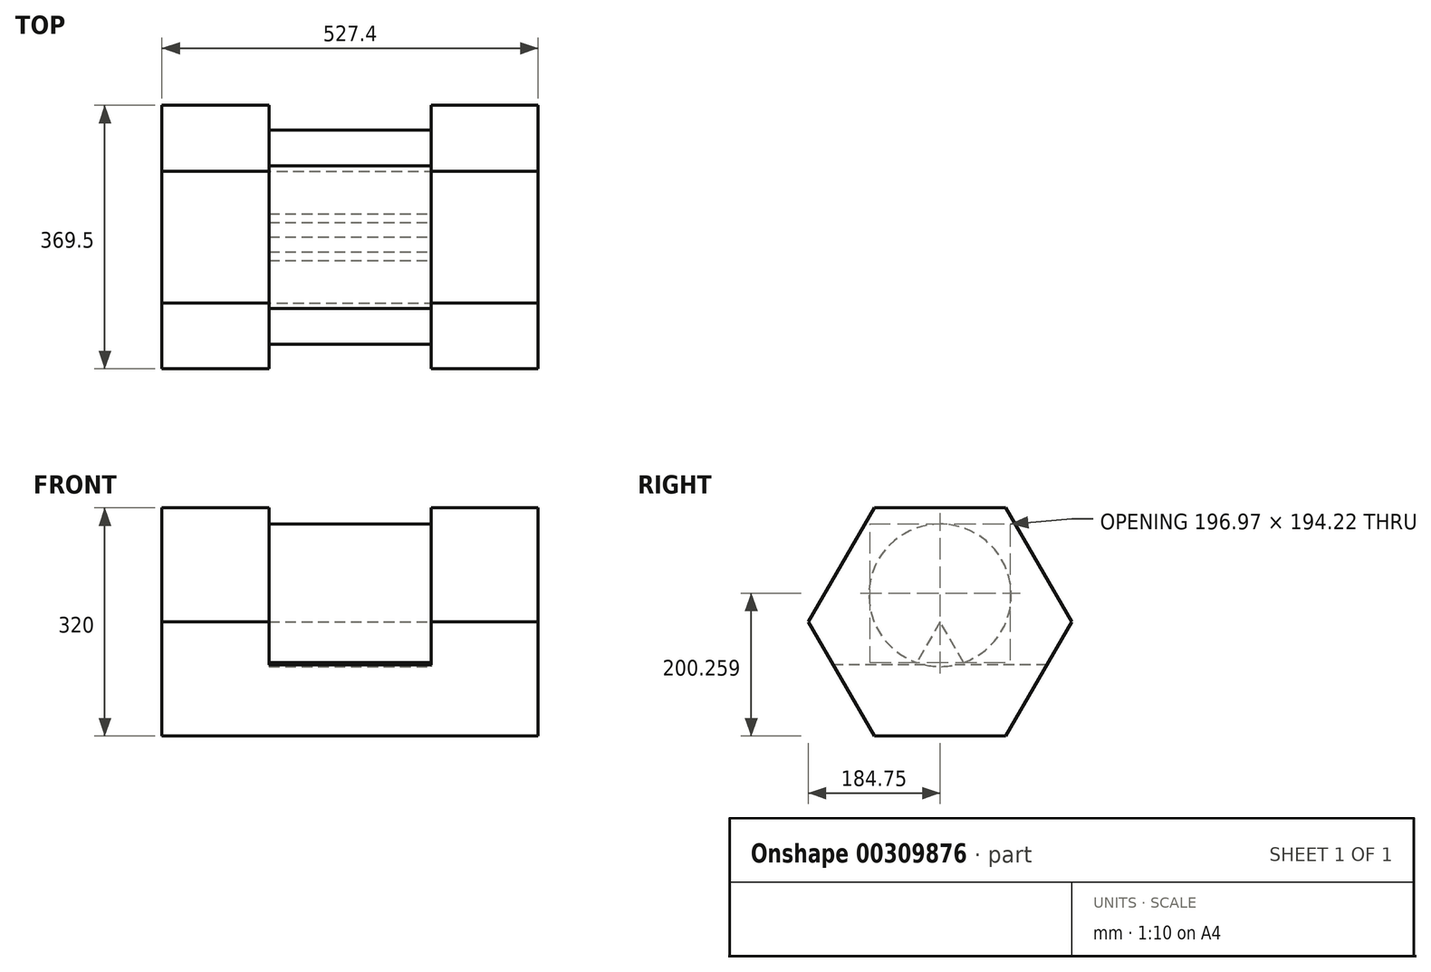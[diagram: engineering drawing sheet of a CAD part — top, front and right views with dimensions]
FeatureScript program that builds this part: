
annotation { "Feature Type Name" : "Feature", "Feature Type Description" : "" }
export const myFeature = defineFeature(function(context is Context, id is Id, definition is map)
    precondition{}
    {
        {
            var Q0;
            Q0=qCreatedBy(makeId("Top.planeOp"),FACE);
            var sketch = newSketch(context, id + "F0", { "sketchPlane" : qUnion([Q0])});
            skLineSegment(sketch, "E0.bottom", {"start": v(463.7, -463.7) * mm, "end": v(-463.7, -463.7) * mm});
            skLineSegment(sketch, "E0.top", {"start": v(463.7, 463.7) * mm, "end": v(-463.7, 463.7) * mm});
            skLineSegment(sketch, "E0.left", {"start": v(463.7, -463.7) * mm, "end": v(463.7, 463.7) * mm});
            skLineSegment(sketch, "E0.right", {"start": v(-463.7, -463.7) * mm, "end": v(-463.7, 463.7) * mm});
            skPoint(sketch, "E0.middle", {"position": v(0, 0) * mm});
            skLineSegment(sketch, "E1", {"start": v(-263.7, -463.7) * mm, "end": v(-263.7, 463.7) * mm});
            skLineSegment(sketch, "E2", {"start": v(263.7, -463.7) * mm, "end": v(263.7, 463.7) * mm});
            skLineSegment(sketch, "E3", {"start": v(-463.7, 263.7) * mm, "end": v(463.7, 263.7) * mm});
            skLineSegment(sketch, "E4", {"start": v(463.7, -263.7) * mm, "end": v(-463.7, -263.7) * mm});
            skSolve(sketch);
        }
        {
            var Q0;
            Q0=sQuery(id+"F0.wireOp",EDGE,"E2");
            cPlane(context, id + "F1", {"entities" : qUnion([Q0]), "cplaneType" : CPlaneType.LINE_ANGLE, "offset" : 25 * mm, "angle" : 90 * degree, "width" : 150 * mm, "height" : 150 * mm});
        }
        {
            var Q0;
            Q0=qCreatedBy(id+"F1.planeOp",FACE);
            var sketch = newSketch(context, id + "F2", { "sketchPlane" : qUnion([Q0])});
            skPoint(sketch, "E5", {"position": v(0, 0) * mm});
            skPoint(sketch, "E6", {"position": v(1245.8, -121.93) * mm});
            skPoint(sketch, "E7.0", {"position": v(-263.7, 0) * mm});
            skPoint(sketch, "E8.0", {"position": v(263.7, 0) * mm});
            skPoint(sketch, "E9", {"position": v(131.85, 0) * mm});
            skLineSegment(sketch, "E10", {"start": v(0, 0) * mm, "end": v(0, 320) * mm});
            skCircle(sketch, "E11.cCircle", {"center": v(0, 160) * mm, "radius": 160 * mm, "construction": true});
            skLineSegment(sketch, "E11.0", {"start": v(92.38, 0) * mm, "end": v(-92.38, 0) * mm});
            skLineSegment(sketch, "E11.1", {"start": v(-92.38, 0) * mm, "end": v(-184.75, 160) * mm});
            skLineSegment(sketch, "E11.2", {"start": v(-184.75, 160) * mm, "end": v(-92.38, 320) * mm});
            skLineSegment(sketch, "E11.3", {"start": v(-92.38, 320) * mm, "end": v(92.38, 320) * mm});
            skLineSegment(sketch, "E11.4", {"start": v(92.38, 320) * mm, "end": v(184.75, 160) * mm});
            skLineSegment(sketch, "E11.5", {"start": v(184.75, 160) * mm, "end": v(92.38, 0) * mm});
            skSolve(sketch);
        }
        {
            var Q0;
            {var subQ2=sQuery(id+"F2.wireOp",EDGE,"E10");Q0=makeQuery(id+"F2.imprint","IMPRINT",FACE,{"disambiguationData":[TD([[makeQuery(id+"F2.imprint","IMPRINT",EDGE,{"derivedFrom":subQ2}),-1.0]])]});}
            var Q1;
            {var subQ3=sQuery(id+"F2.wireOp",EDGE,"E10");Q1=makeQuery(id+"F2.imprint","IMPRINT",FACE,{"disambiguationData":[TD([[makeQuery(id+"F2.imprint","IMPRINT",EDGE,{"derivedFrom":subQ3}),1.0]])]});}
            extrude(context, id + "F3", {"entities" : qUnion([Q0, Q1]), "oppositeDirection" : true, "depth" : 150 * mm});
        }
        {
            var Q0;
            Q0=makeQuery(id+"F3.opExtrude","SWEPT_BODY",BODY,{"disambiguationData":[OSD([sQuery(id+"F2.wireOp",EDGE,"E11.0"),sQuery(id+"F2.wireOp",EDGE,"E11.1"),sQuery(id+"F2.wireOp",EDGE,"E11.2"),sQuery(id+"F2.wireOp",EDGE,"E11.3"),sQuery(id+"F2.wireOp",EDGE,"E11.4"),sQuery(id+"F2.wireOp",EDGE,"E11.5")])]});
            var Q1;
            Q1=qCreatedBy(makeId("Right.planeOp"),FACE);
            mirror(context, id + "F4", {"entities" : qUnion([Q0]), "mirrorPlane" : qUnion([Q1])});
        }
        {
            var Q0;
            Q0=makeQuery(id+"F3.opExtrude","CAP_FACE",FACE,{"disambiguationData":[OSD([sQuery(id+"F2.wireOp",EDGE,"E11.0"),sQuery(id+"F2.wireOp",EDGE,"E11.1"),sQuery(id+"F2.wireOp",EDGE,"E11.2"),sQuery(id+"F2.wireOp",EDGE,"E11.3"),sQuery(id+"F2.wireOp",EDGE,"E11.4"),sQuery(id+"F2.wireOp",EDGE,"E11.5")])],"isStart":false});
            var sketch = newSketch(context, id + "F5", { "sketchPlane" : qUnion([Q0])});
            skLineSegment(sketch, "E12", {"start": v(-92.38, 0) * mm, "end": v(92.38, 320) * mm});
            skLineSegment(sketch, "E13", {"start": v(-184.75, 160) * mm, "end": v(184.75, 160) * mm});
            skPoint(sketch, "E14", {"position": v(0, 160) * mm});
            skLineSegment(sketch, "E15", {"start": v(0, 160) * mm, "end": v(92.38, 0) * mm});
            skLineSegment(sketch, "E16", {"start": v(0, 160) * mm, "end": v(0, 320) * mm});
            skLineSegment(sketch, "E17", {"start": v(-150, 99.8) * mm, "end": v(150, 99.8) * mm});
            skPoint(sketch, "E18", {"position": v(0, 197.49) * mm});
            skCircle(sketch, "E19", {"center": v(0, 197.49) * mm, "radius": 99.88 * mm});
            skSolve(sketch);
        }
        {
            var Q0;
            {var subQ1=makeQuery(id+"F3.opExtrude","CAP_EDGE",EDGE,{"disambiguationData":[OSD([sQuery(id+"F2.wireOp",EDGE,"E11.5")])],"isStart":false});var subQ3=sQuery(id+"F5.wireOp",EDGE,"E17");var subQ5=makeQuery(id+"F5.imprint","INTERSECT",VERTEX,{"derivedFrom":[subQ1,subQ3]});Q0=makeQuery(id+"F5.imprint","IMPRINT",FACE,{"disambiguationData":[TD([[makeQuery(id+"F5.imprint","IMPRINT",EDGE,{"disambiguationData":[TD([[subQ5,-1.0]])],"derivedFrom":subQ3}),-1.0]])]});}
            var Q1;
            {var subQ1=makeQuery(id+"F3.opExtrude","CAP_EDGE",EDGE,{"disambiguationData":[OSD([sQuery(id+"F2.wireOp",EDGE,"E11.0")])],"isStart":false});Q1=makeQuery(id+"F5.imprint","IMPRINT",FACE,{"disambiguationData":[TD([[makeQuery(id+"F5.imprint","IMPRINT",EDGE,{"derivedFrom":subQ1}),1.0]])]});}
            var Q2;
            {var subQ1=makeQuery(id+"F3.opExtrude","CAP_EDGE",EDGE,{"disambiguationData":[OSD([sQuery(id+"F2.wireOp",EDGE,"E11.1")])],"isStart":false});var subQ3=sQuery(id+"F5.wireOp",EDGE,"E17");var subQ5=makeQuery(id+"F5.imprint","INTERSECT",VERTEX,{"derivedFrom":[subQ1,subQ3]});Q2=makeQuery(id+"F5.imprint","IMPRINT",FACE,{"disambiguationData":[TD([[makeQuery(id+"F5.imprint","IMPRINT",EDGE,{"disambiguationData":[TD([[subQ5,1.0]])],"derivedFrom":subQ3}),-1.0]])]});}
            var Q3;
            Q3=makeQuery(id+"F4.opPattern","COPY",FACE,{"derivedFrom":makeQuery(id+"F3.opExtrude","CAP_FACE",FACE,{"disambiguationData":[OSD([sQuery(id+"F2.wireOp",EDGE,"E11.0"),sQuery(id+"F2.wireOp",EDGE,"E11.1"),sQuery(id+"F2.wireOp",EDGE,"E11.2"),sQuery(id+"F2.wireOp",EDGE,"E11.3"),sQuery(id+"F2.wireOp",EDGE,"E11.4"),sQuery(id+"F2.wireOp",EDGE,"E11.5")])],"isStart":false}),"instanceName":"1"});
            extrude(context, id + "F6", {"entities" : qUnion([Q0, Q1, Q2]), "operationType" : NewBodyOperationType.ADD, "endBound" : BoundingType.UP_TO_SURFACE, "endBoundEntityFace" : qUnion([Q3]), "depth" : 25 * mm});
        }
        {
            var Q0;
            {var subQ1=sQuery(id+"F5.wireOp",EDGE,"E13");var subQ3=sQuery(id+"F5.wireOp",EDGE,"E19");var subQ4=makeQuery(id+"F5.imprint","INTERSECT",VERTEX,{"disambiguationData":[OD(0.0)],"derivedFrom":[subQ1,subQ3]});Q0=makeQuery(id+"F5.imprint","IMPRINT",FACE,{"disambiguationData":[TD([[makeQuery(id+"F5.imprint","IMPRINT",EDGE,{"disambiguationData":[TD([[subQ4,1.0]])],"derivedFrom":subQ3}),1.0]])]});}
            var Q1;
            {var subQ1=sQuery(id+"F5.wireOp",EDGE,"E12");var subQ3=sQuery(id+"F5.wireOp",EDGE,"E19");var subQ4=makeQuery(id+"F5.imprint","INTERSECT",VERTEX,{"disambiguationData":[OD(1.0)],"derivedFrom":[subQ1,subQ3]});Q1=makeQuery(id+"F5.imprint","IMPRINT",FACE,{"disambiguationData":[TD([[makeQuery(id+"F5.imprint","IMPRINT",EDGE,{"disambiguationData":[TD([[subQ4,-1.0]])],"derivedFrom":subQ3}),1.0]])]});}
            var Q2;
            {var subQ1=sQuery(id+"F5.wireOp",EDGE,"E12");var subQ3=sQuery(id+"F5.wireOp",EDGE,"E19");var subQ4=makeQuery(id+"F5.imprint","INTERSECT",VERTEX,{"disambiguationData":[OD(1.0)],"derivedFrom":[subQ1,subQ3]});Q2=makeQuery(id+"F5.imprint","IMPRINT",FACE,{"disambiguationData":[TD([[makeQuery(id+"F5.imprint","IMPRINT",EDGE,{"disambiguationData":[TD([[subQ4,1.0]])],"derivedFrom":subQ3}),1.0]])]});}
            var Q3;
            {var subQ1=sQuery(id+"F5.wireOp",EDGE,"E13");var subQ3=sQuery(id+"F5.wireOp",EDGE,"E19");var subQ4=makeQuery(id+"F5.imprint","INTERSECT",VERTEX,{"disambiguationData":[OD(1.0)],"derivedFrom":[subQ1,subQ3]});Q3=makeQuery(id+"F5.imprint","IMPRINT",FACE,{"disambiguationData":[TD([[makeQuery(id+"F5.imprint","IMPRINT",EDGE,{"disambiguationData":[TD([[subQ4,1.0]])],"derivedFrom":subQ3}),1.0]])]});}
            var Q4;
            {var subQ1=sQuery(id+"F5.wireOp",EDGE,"E12");var subQ3=sQuery(id+"F5.wireOp",EDGE,"E19");var subQ4=makeQuery(id+"F5.imprint","INTERSECT",VERTEX,{"disambiguationData":[OD(0.0)],"derivedFrom":[subQ1,subQ3]});Q4=makeQuery(id+"F5.imprint","IMPRINT",FACE,{"disambiguationData":[TD([[makeQuery(id+"F5.imprint","IMPRINT",EDGE,{"disambiguationData":[TD([[subQ4,1.0]])],"derivedFrom":subQ3}),1.0]])]});}
            var Q5;
            Q5=makeQuery(id+"F4.opPattern","COPY",FACE,{"derivedFrom":makeQuery(id+"F3.opExtrude","CAP_FACE",FACE,{"disambiguationData":[OSD([sQuery(id+"F2.wireOp",EDGE,"E11.0"),sQuery(id+"F2.wireOp",EDGE,"E11.1"),sQuery(id+"F2.wireOp",EDGE,"E11.2"),sQuery(id+"F2.wireOp",EDGE,"E11.3"),sQuery(id+"F2.wireOp",EDGE,"E11.4"),sQuery(id+"F2.wireOp",EDGE,"E11.5")])],"isStart":false}),"instanceName":"1"});
            extrude(context, id + "F7", {"entities" : qUnion([Q0, Q1, Q2, Q3, Q4]), "operationType" : NewBodyOperationType.ADD, "endBound" : BoundingType.UP_TO_SURFACE, "endBoundEntityFace" : qUnion([Q5]), "depth" : 25 * mm});
        }
        {
            var Q0;
            Q0=makeQuery(id+"F3.opExtrude","CAP_FACE",FACE,{"disambiguationData":[OSD([sQuery(id+"F2.wireOp",EDGE,"E11.0"),sQuery(id+"F2.wireOp",EDGE,"E11.1"),sQuery(id+"F2.wireOp",EDGE,"E11.2"),sQuery(id+"F2.wireOp",EDGE,"E11.3"),sQuery(id+"F2.wireOp",EDGE,"E11.4"),sQuery(id+"F2.wireOp",EDGE,"E11.5")])],"isStart":true});
            var sketch = newSketch(context, id + "F8", { "sketchPlane" : qUnion([Q0])});
            skLineSegment(sketch, "E20", {"start": v(-184.75, 160) * mm, "end": v(184.75, 160) * mm});
            skLineSegment(sketch, "E21", {"start": v(-184.75, 160) * mm, "end": v(-92.38, 320) * mm});
            skLineSegment(sketch, "E22", {"start": v(-92.38, 320) * mm, "end": v(92.38, 320) * mm});
            skLineSegment(sketch, "E23", {"start": v(92.38, 320) * mm, "end": v(184.75, 160) * mm});
            skSolve(sketch);
        }
    });
